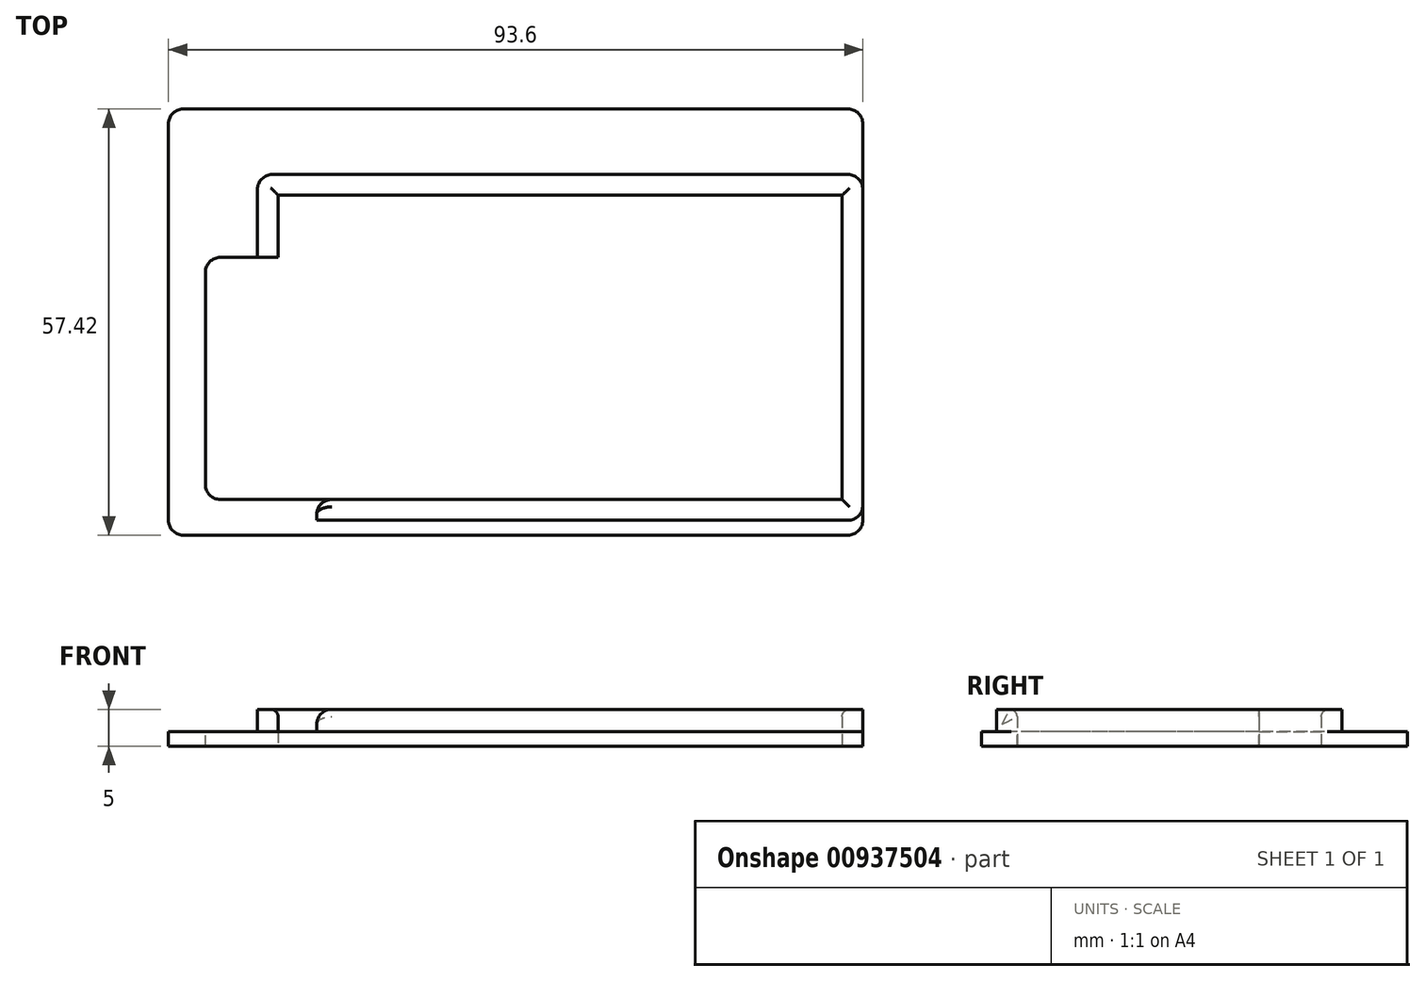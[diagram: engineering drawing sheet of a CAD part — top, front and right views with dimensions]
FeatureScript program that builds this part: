
annotation { "Feature Type Name" : "Feature", "Feature Type Description" : "" }
export const myFeature = defineFeature(function(context is Context, id is Id, definition is map)
    precondition{}
    {
        {
            var Q0;
            Q0=qCreatedBy(makeId("Top.planeOp"),FACE);
            var sketch = newSketch(context, id + "F0", { "sketchPlane" : qUnion([Q0])});
            skLineSegment(sketch, "E0.bottom", {"start": v(-44.2, 28.71) * mm, "end": v(49.4, 28.71) * mm});
            skLineSegment(sketch, "E0.top", {"start": v(-44.2, -28.71) * mm, "end": v(49.4, -28.71) * mm});
            skLineSegment(sketch, "E0.left", {"start": v(-44.2, 28.71) * mm, "end": v(-44.2, -28.71) * mm});
            skLineSegment(sketch, "E0.right", {"start": v(49.4, 28.72) * mm, "end": v(49.4, -28.71) * mm});
            skSolve(sketch);
        }
        {
            var Q0;
            Q0=makeQuery(id+"F0.imprint","IMPRINT",FACE,{"disambiguationData":[TD([[makeQuery(id+"F0.imprint","IMPRINT",EDGE,{"derivedFrom":sQuery(id+"F0.wireOp",EDGE,"E0.bottom")}),-1.0]])]});
            extrude(context, id + "F1", {"entities" : qUnion([Q0]), "oppositeDirection" : true, "depth" : 2 * mm, "offsetDistance" : 25 * mm});
        }
        {
            var Q0;
            Q0=makeQuery(id+"F1.opExtrude","CAP_FACE",FACE,{"disambiguationData":[OSD([sQuery(id+"F0.wireOp",EDGE,"E0.bottom"),sQuery(id+"F0.wireOp",EDGE,"E0.top"),sQuery(id+"F0.wireOp",EDGE,"E0.left"),sQuery(id+"F0.wireOp",EDGE,"E0.right")])],"isStart":true});
            var sketch = newSketch(context, id + "F2", { "sketchPlane" : qUnion([Q0])});
            skLineSegment(sketch, "E1.bottom", {"start": v(46.6, -23.91) * mm, "end": v(-29.4, -23.91) * mm});
            skLineSegment(sketch, "E1.top", {"start": v(46.6, 17.09) * mm, "end": v(-29.4, 17.09) * mm});
            skLineSegment(sketch, "E1.left", {"start": v(46.6, -23.91) * mm, "end": v(46.6, 17.09) * mm});
            skLineSegment(sketch, "E1.right", {"start": v(-29.4, -23.91) * mm, "end": v(-29.4, 17.09) * mm});
            skPoint(sketch, "E2", {"position": v(-31.8, 0) * mm});
            skPoint(sketch, "E3", {"position": v(46.6, -3.41) * mm});
            skPoint(sketch, "E4", {"position": v(8.6, 17.09) * mm});
            skPoint(sketch, "E5", {"position": v(8.6, -23.91) * mm});
            skSolve(sketch);
        }
        {
            var Q0;
            Q0=makeQuery(id+"F2.imprint","IMPRINT",FACE,{"disambiguationData":[TD([[makeQuery(id+"F2.imprint","IMPRINT",EDGE,{"derivedFrom":makeQuery(id+"F1.opExtrude","CAP_EDGE",EDGE,{"disambiguationData":[OSD([sQuery(id+"F0.wireOp",EDGE,"E0.bottom")])],"isStart":true})}),-1.0]])]});
            var sketch = newSketch(context, id + "F3", { "sketchPlane" : qUnion([Q0])});
            skPoint(sketch, "E6.0", {"position": v(-29.4, 17.09) * mm});
            skLineSegment(sketch, "E7.0", {"start": v(46.6, 17.09) * mm, "end": v(-29.5, 17.09) * mm});
            skLineSegment(sketch, "E8.0", {"start": v(46.6, -23.91) * mm, "end": v(-24.2, -23.91) * mm});
            skPoint(sketch, "E9", {"position": v(-29.4, 8.72) * mm});
            skLineSegment(sketch, "E10", {"start": v(-29.4, 8.72) * mm, "end": v(-32.2, 8.72) * mm, "construction": true});
            skLineSegment(sketch, "E11", {"start": v(-32.2, 8.72) * mm, "end": v(-32.2, 19.89) * mm});
            skLineSegment(sketch, "E12", {"start": v(-32.2, 19.89) * mm, "end": v(49.4, 19.89) * mm});
            skLineSegment(sketch, "E13.0", {"start": v(49.4, 28.71) * mm, "end": v(49.4, -28.71) * mm, "construction": true});
            skLineSegment(sketch, "E14", {"start": v(-24.2, -26.72) * mm, "end": v(49.4, -26.71) * mm});
            skLineSegment(sketch, "E15", {"start": v(49.4, -26.71) * mm, "end": v(49.4, -23.91) * mm, "construction": true});
            skLineSegment(sketch, "E16", {"start": v(-24.2, -26.72) * mm, "end": v(-24.2, -23.91) * mm, "construction": true});
            skLineSegment(sketch, "E17", {"start": v(-24.2, -26.72) * mm, "end": v(-24.2, -23.91) * mm});
            skLineSegment(sketch, "E18", {"start": v(49.4, -26.71) * mm, "end": v(49.4, -23.91) * mm});
            skLineSegment(sketch, "E19", {"start": v(-29.4, 8.72) * mm, "end": v(-32.2, 8.72) * mm});
            skLineSegment(sketch, "E20", {"start": v(49.4, 19.89) * mm, "end": v(49.4, 17.09) * mm});
            skLineSegment(sketch, "E21", {"start": v(-32.2, 8.72) * mm, "end": v(-29.4, 8.72) * mm});
            skPoint(sketch, "E22.0.end.orphan", {"position": v(-31.8, 17.09) * mm});
            skLineSegment(sketch, "E23", {"start": v(-29.4, 8.72) * mm, "end": v(-29.4, 17.09) * mm});
            skLineSegment(sketch, "E24", {"start": v(46.6, 17.09) * mm, "end": v(46.6, -23.91) * mm});
            skLineSegment(sketch, "E25", {"start": v(49.4, 17.09) * mm, "end": v(49.4, -23.91) * mm});
            skSolve(sketch);
        }
        {
            var Q0;
            Q0 = qSketchRegion(id + "F3", true);
            extrude(context, id + "F4", {"entities" : qUnion([Q0]), "operationType" : NewBodyOperationType.ADD, "depth" : 3 * mm, "offsetDistance" : 25 * mm});
        }
        {
            var Q0;
            Q0=makeQuery(id+"F4.opExtrude","CAP_EDGE",EDGE,{"disambiguationData":[OSD([sQuery(id+"F3.wireOp",EDGE,"E7.0")])],"isStart":false});
            var Q1;
            Q1=makeQuery(id+"F4.opExtrude","CAP_EDGE",EDGE,{"disambiguationData":[OSD([sQuery(id+"F3.wireOp",EDGE,"E23")])],"isStart":false});
            var Q2;
            Q2=makeQuery(id+"F4.opExtrude","CAP_EDGE",EDGE,{"disambiguationData":[OSD([sQuery(id+"F3.wireOp",EDGE,"E8.0")])],"isStart":false});
            var Q3;
            Q3=makeQuery(id+"F4.opExtrude","CAP_EDGE",EDGE,{"disambiguationData":[OSD([sQuery(id+"F2.wireOp",EDGE,"E1.left")])],"isStart":false});
            var Q4;
            Q4=makeQuery(id+"F4.opExtrude","CAP_EDGE",EDGE,{"disambiguationData":[OSD([sQuery(id+"F3.wireOp",EDGE,"E24")])],"isStart":false});
            fillet(context, id + "F5", {"entities" : qUnion([Q0, Q1, Q2, Q3, Q4]), "radius" : 1 * mm, "tangentPropagation" : true, "allowEdgeOverflow" : false});
        }
        {
            var Q0;
            Q0=makeQuery(id+"F2.imprint","IMPRINT",FACE,{"disambiguationData":[TD([[makeQuery(id+"F2.imprint","IMPRINT",EDGE,{"derivedFrom":sQuery(id+"F2.wireOp",EDGE,"E1.bottom")}),-1.0]])]});
            extrude(context, id + "F6", {"entities" : qUnion([Q0]), "operationType" : NewBodyOperationType.REMOVE, "oppositeDirection" : true, "depth" : 25 * mm, "offsetDistance" : 25 * mm});
        }
        {
            var Q0;
            Q0=makeQuery(id+"F2.imprint","IMPRINT",FACE,{"disambiguationData":[TD([[makeQuery(id+"F2.imprint","IMPRINT",EDGE,{"derivedFrom":sQuery(id+"F2.wireOp",EDGE,"E1.bottom")}),1.0]])]});
            var sketch = newSketch(context, id + "F7", { "sketchPlane" : qUnion([Q0])});
            skPoint(sketch, "E26.0", {"position": v(-29.4, 8.72) * mm});
            skLineSegment(sketch, "E27.0", {"start": v(-44.2, 26.72) * mm, "end": v(-44.2, -28.71) * mm, "construction": true});
            skLineSegment(sketch, "E28.0", {"start": v(-44.2, -28.71) * mm, "end": v(47.4, -28.71) * mm, "construction": true});
            skLineSegment(sketch, "E29", {"start": v(-29.4, 8.72) * mm, "end": v(-39.2, 8.72) * mm});
            skLineSegment(sketch, "E30", {"start": v(-39.2, 8.72) * mm, "end": v(-39.2, -23.91) * mm});
            skPoint(sketch, "E31.0", {"position": v(-24.2, -23.91) * mm});
            skLineSegment(sketch, "E32", {"start": v(-39.2, -23.91) * mm, "end": v(-29.4, -23.91) * mm});
            skLineSegment(sketch, "E33", {"start": v(-29.4, 8.71) * mm, "end": v(-29.4, -23.91) * mm});
            skSolve(sketch);
        }
        {
            var Q0;
            Q0=makeQuery(id+"F7.imprint","IMPRINT",FACE,{"disambiguationData":[TD([[makeQuery(id+"F7.imprint","IMPRINT",EDGE,{"derivedFrom":sQuery(id+"F7.wireOp",EDGE,"E29")}),1.0]])]});
            extrude(context, id + "F8", {"entities" : qUnion([Q0]), "operationType" : NewBodyOperationType.REMOVE, "oppositeDirection" : true, "depth" : 25 * mm, "offsetDistance" : 25 * mm});
        }
        {
            var Q0;
            Q0=makeQuery(id+"F1.opExtrude","SWEPT_EDGE",EDGE,{"disambiguationData":[OSD([sQuery(id+"F0.wireOp",EDGE,"E0.top"),sQuery(id+"F0.wireOp",EDGE,"E0.right")])]});
            var Q1;
            Q1=makeQuery(id+"F1.opExtrude","SWEPT_EDGE",EDGE,{"disambiguationData":[OSD([sQuery(id+"F0.wireOp",EDGE,"E0.bottom"),sQuery(id+"F0.wireOp",EDGE,"E0.right")])]});
            var Q2;
            Q2=makeQuery(id+"F1.opExtrude","SWEPT_EDGE",EDGE,{"disambiguationData":[OSD([sQuery(id+"F0.wireOp",EDGE,"E0.bottom"),sQuery(id+"F0.wireOp",EDGE,"E0.left")])]});
            var Q3;
            Q3=makeQuery(id+"F1.opExtrude","SWEPT_EDGE",EDGE,{"disambiguationData":[OSD([sQuery(id+"F0.wireOp",EDGE,"E0.top"),sQuery(id+"F0.wireOp",EDGE,"E0.left")])]});
            var Q4;
            {var subQ0=sQuery(id+"F2.wireOp",EDGE,"E1.right");Q4=makeQuery(id+"F8.boolean.opBoolean","MERGE",EDGE,{"derivedFrom":[makeQuery(id+"F4.opExtrude","SWEPT_EDGE",EDGE,{"disambiguationData":[OSD([subQ0,sQuery(id+"F3.wireOp",EDGE,"E21"),sQuery(id+"F3.wireOp",EDGE,"E23")])]})],"fromTools":[makeQuery(id+"F8.opExtrude","SWEPT_EDGE",EDGE,{"disambiguationData":[OSD([subQ0,sQuery(id+"F7.wireOp",EDGE,"E29"),sQuery(id+"F7.wireOp",EDGE,"E33")])]})]});}
            var Q5;
            Q5=makeQuery(id+"F8.boolean.opBoolean","COPY",EDGE,{"derivedFrom":makeQuery(id+"F8.opExtrude","SWEPT_EDGE",EDGE,{"disambiguationData":[OSD([sQuery(id+"F7.wireOp",EDGE,"E29"),sQuery(id+"F7.wireOp",EDGE,"E30")])]})});
            var Q6;
            Q6=makeQuery(id+"F8.boolean.opBoolean","COPY",EDGE,{"derivedFrom":makeQuery(id+"F8.opExtrude","SWEPT_EDGE",EDGE,{"disambiguationData":[OSD([sQuery(id+"F7.wireOp",EDGE,"E30"),sQuery(id+"F7.wireOp",EDGE,"E32")])]})});
            var Q7;
            Q7=makeQuery(id+"F4.opExtrude","SWEPT_EDGE",EDGE,{"disambiguationData":[OSD([sQuery(id+"F3.wireOp",EDGE,"E11"),sQuery(id+"F3.wireOp",EDGE,"E12")])]});
            var Q8;
            Q8=makeQuery(id+"F4.opExtrude","SWEPT_EDGE",EDGE,{"disambiguationData":[OSD([sQuery(id+"F0.wireOp",EDGE,"E0.right"),sQuery(id+"F3.wireOp",EDGE,"E12"),sQuery(id+"F3.wireOp",EDGE,"E20")])]});
            var Q9;
            Q9=makeQuery(id+"F4.opExtrude","SWEPT_EDGE",EDGE,{"disambiguationData":[OSD([sQuery(id+"F0.wireOp",EDGE,"E0.right"),sQuery(id+"F3.wireOp",EDGE,"E14"),sQuery(id+"F3.wireOp",EDGE,"E18")])]});
            var Q10;
            Q10=makeQuery(id+"F4.opExtrude","SWEPT_EDGE",EDGE,{"disambiguationData":[OSD([sQuery(id+"F2.wireOp",EDGE,"E1.bottom"),sQuery(id+"F3.wireOp",EDGE,"E8.0"),sQuery(id+"F3.wireOp",EDGE,"E17")])]});
            fillet(context, id + "F9", {"entities" : qUnion([Q0, Q1, Q2, Q3, Q4, Q5, Q6, Q7, Q8, Q9, Q10]), "radius" : 2 * mm, "tangentPropagation" : true, "allowEdgeOverflow" : false});
        }
    });
